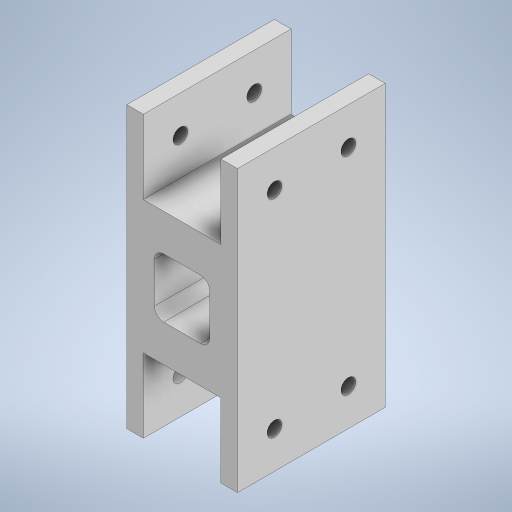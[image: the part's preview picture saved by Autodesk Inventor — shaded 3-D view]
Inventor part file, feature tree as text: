
AUTODESK INVENTOR PART (.ipt)
format: ipt  version: 2024 (Build 280153000, 153)  size: 293,888 bytes
history: native  units: in
note: dims shown in document units (in); Inventor stores cm internally (conversion verified against a paired STEP export)
features: other x3, extrude x3, sketch x2, projected_geometry x2, fillet x1, hole x1
ambient origin geometry x8: Origin, YZ Plane, XZ Plane, XY Plane, X Axis, Y Axis, Z Axis, Center Point
bodies: Solid1 (feature_tree)
feature tree (12):
  other  "Arm_H-Bracket"
  extrude  "HBracket_3DShape"  Depth=3.8in
  extrude  "MiddleHole"  Depth=1.0in
  fillet  "RoundedInside"  Radius=0.25in
  hole  "Screw Holes"  [1 undecoded]
  extrude  "GapSpace"  Depth=1.0in
  other  "Bracket-CrossArea"
  sketch  "Sketch2"  dims[d3=0.25in d4=3.8in]
  sketch  "Sketch4"  dims[d5=1.0in d6=1.0in d7=0.25in d8=2.0in d9=0.0in d10=1.0in d11=0.5in d12=0.5in d15=0.0in d16=0.0in d29=0.375in d30=0.375in d41=0.201in d42=0.75in d43=0.563in d44=0.12in d45=0.5635in d46=1.0in d47=0.8108in d48=0.5in d49=0.5in d50=0.7874in d52=1.0in d53=0.7874in d55=2.8in d58=0.025in d59=0.025in d62=0.025in d63=0.025in d65=0.0in d66=0.0in d69=0.125in]
  projected_geometry  "Projected Loop1"
  other  "GapSpacing"
  projected_geometry  "Projected Loop2"
note: 1 required parameter value undecoded (feature->parameter linkage not recoverable at this tier; creation-order binding heuristic only, values carry confidence <= 0.55)
